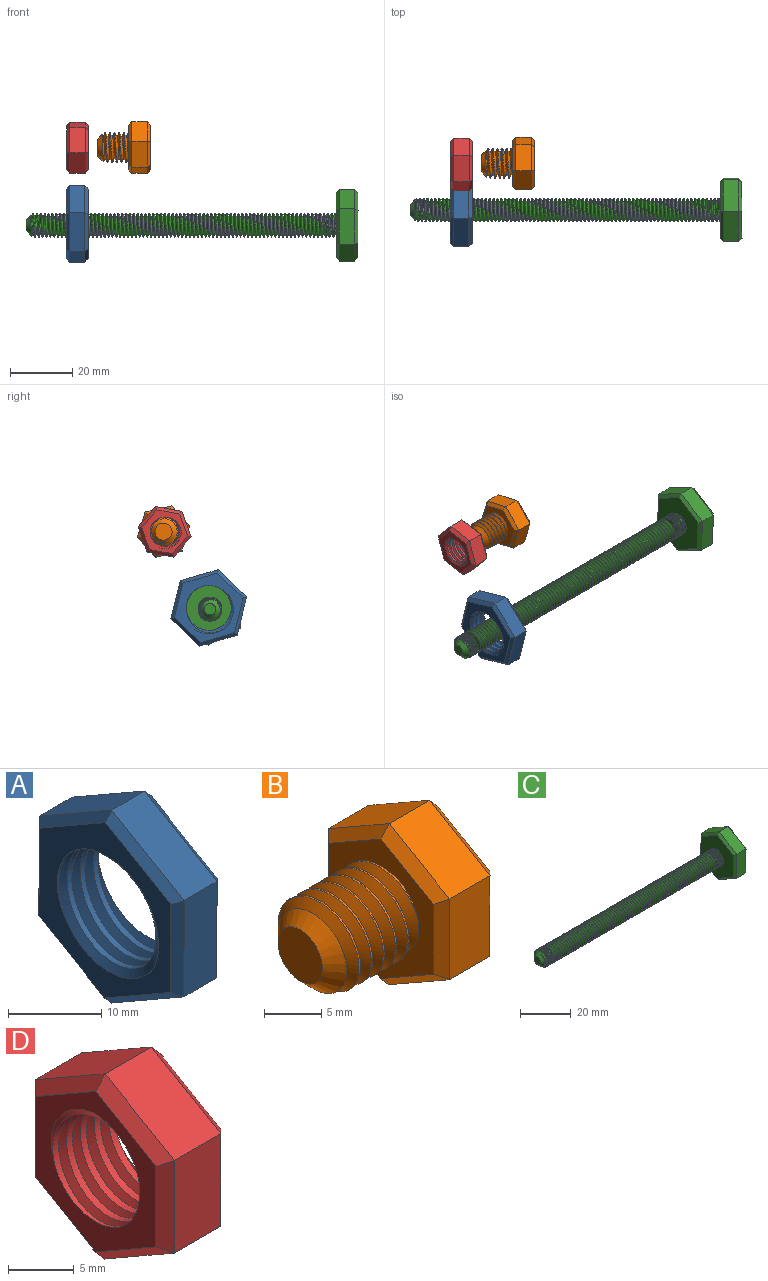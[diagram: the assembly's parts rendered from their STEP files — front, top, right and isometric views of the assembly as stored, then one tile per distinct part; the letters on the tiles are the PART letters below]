
ASSEMBLY  parts=4 mates=2
PART A: 23 faces, bbox 9.3x22.7x26 mm
  f0: cylinder r=7.24mm len=14.48mm, axis (1,0,0), area 111.6mm2, adj f7,f8,f21,f22
  f1: plane 10.98x6.38mm, normal (0,-0.5,0.86), area 63.5mm2, adj f2,f6,f14,f18
  f2: plane 12.7x5mm, normal (0,-1,0), area 63.5mm2, adj f1,f3,f12,f16
  f3: plane 11.02x6.32mm, normal (0,-0.5,-0.87), area 63.5mm2, adj f2,f4,f10,f15
  f4: plane 10.98x6.38mm, normal (0,0.5,-0.86), area 63.5mm2, adj f3,f5,f9,f17
  f5: plane 12.7x5mm, normal (0,1,0), area 63.5mm2, adj f4,f6,f11,f19
  f6: plane 11.02x6.32mm, normal (0,0.5,0.87), area 63.5mm2, adj f1,f5,f13,f20
  f7: plane 23.73x20.67mm, normal (-1,0,0), area 164.4mm2, adj f0,f9,f10,f11,f12,f13,f14,f21
  f8: plane 23.73x20.67mm, normal (1,0,0), area 164.4mm2, adj f0,f15,f16,f17,f18,f19,f20,f21
  f9: plane 10.99x6.96mm, normal (-0.71,0.36,-0.61), area 17.1mm2, adj f4,f7,f10,f11
  f10: plane 11.02x6.9mm, normal (-0.71,-0.35,-0.61), area 17.1mm2, adj f3,f7,f9,f12
  f11: plane 12.7x1.03mm, normal (-0.71,0.71,0), area 17.1mm2, adj f5,f7,f9,f13
  f12: plane 12.7x1.03mm, normal (-0.71,-0.71,0), area 17.1mm2, adj f2,f7,f10,f14
  f13: plane 11.02x6.9mm, normal (-0.71,0.35,0.61), area 17.1mm2, adj f6,f7,f11,f14
  f14: plane 10.99x6.96mm, normal (-0.71,-0.36,0.61), area 17.1mm2, adj f1,f7,f12,f13
  f15: plane 11.02x6.9mm, normal (0.71,-0.35,-0.61), area 17.1mm2, adj f3,f8,f16,f17
  f16: plane 12.7x1.03mm, normal (0.71,-0.71,0), area 17.1mm2, adj f2,f8,f15,f18
  f17: plane 10.99x6.96mm, normal (0.71,0.36,-0.61), area 17.1mm2, adj f4,f8,f15,f19
  f18: plane 10.99x6.96mm, normal (0.71,-0.36,0.61), area 17.1mm2, adj f1,f8,f16,f20
  f19: plane 12.7x1.03mm, normal (0.71,0.71,0), area 17.1mm2, adj f5,f8,f17,f20
  f20: plane 11.02x6.9mm, normal (0.71,0.35,0.61), area 17.1mm2, adj f6,f8,f18,f19
  f21: bspline ~19.31x16.73mm, area 223mm2, adj f0,f7,f8,f22
  f22: bspline ~19.31x16.73mm, area 223mm2, adj f0,f7,f8,f21
PART B: 25 faces, bbox 17.8x15.9x18.1 mm
  f0: cylinder r=4.75mm len=9.5mm, axis (1,0,0), area 28.1mm2, adj f1,f2,f4,f12
  f1: bspline ~10.97x9.91mm, area 196.7mm2, adj f0,f2,f4,f12
  f2: bspline ~10.97x10.66mm, area 196.6mm2, adj f0,f1,f4,f12
  f3: plane 5.5x5.5mm, normal (-1,0,0), area 23.8mm2, adj f4
  f4: cone r=4.75mm half-angle=45deg, axis (1,0,0), area 47.4mm2, adj f0,f1,f2,f3
  f5: plane 7.48x5mm, normal (0,-0.5,0.86), area 43.3mm2, adj f6,f10,f18,f22
  f6: plane 8.66x5mm, normal (0,-1,0), area 43.3mm2, adj f5,f7,f16,f20
  f7: plane 7.52x5mm, normal (0,-0.5,-0.87), area 43.3mm2, adj f6,f8,f14,f19
  f8: plane 7.48x5mm, normal (0,0.5,-0.86), area 43.3mm2, adj f7,f9,f13,f21
  f9: plane 8.66x5mm, normal (0,1,0), area 43.3mm2, adj f8,f10,f15,f23
  f10: plane 7.52x5mm, normal (0,0.5,0.87), area 43.3mm2, adj f5,f9,f17,f24
  f11: plane 15.01x13.03mm, normal (1,0,0), area 146.4mm2, adj f13,f14,f15,f16,f17,f18
  f12: plane 15.83x13.85mm, normal (-1,0,0), area 89.2mm2, adj f0,f1,f2,f19,f20,f21,f22,f23
  f13: plane 7.49x4.93mm, normal (0.71,0.36,-0.61), area 11.4mm2, adj f8,f11,f14,f15
  f14: plane 7.52x4.88mm, normal (0.71,-0.35,-0.61), area 11.4mm2, adj f7,f11,f13,f16
  f15: plane 8.66x1.03mm, normal (0.71,0.71,0), area 11.4mm2, adj f9,f11,f13,f17
  f16: plane 8.66x1.03mm, normal (0.71,-0.71,0), area 11.4mm2, adj f6,f11,f14,f18
  f17: plane 7.52x4.88mm, normal (0.71,0.35,0.61), area 11.4mm2, adj f10,f11,f15,f18
  f18: plane 7.49x4.93mm, normal (0.71,-0.36,0.61), area 11.4mm2, adj f5,f11,f16,f17
  f19: plane 7.52x4.88mm, normal (-0.71,-0.35,-0.61), area 11.4mm2, adj f7,f12,f20,f21
  f20: plane 8.66x1.03mm, normal (-0.71,-0.71,0), area 11.4mm2, adj f6,f12,f19,f22
  f21: plane 7.49x4.93mm, normal (-0.71,0.36,-0.61), area 11.4mm2, adj f8,f12,f19,f23
  f22: plane 7.49x4.93mm, normal (-0.71,-0.36,0.61), area 11.4mm2, adj f5,f12,f20,f24
  f23: plane 8.66x1.03mm, normal (-0.71,0.71,0), area 11.4mm2, adj f9,f12,f21,f24
  f24: plane 7.52x4.88mm, normal (-0.71,0.35,0.61), area 11.4mm2, adj f10,f12,f22,f23
PART C: 25 faces, bbox 107.7x20.7x23.8 mm
  f0: cylinder r=3.84mm len=98mm, axis (1,0,0), area 1496mm2, adj f1,f2,f4,f12
  f1: bspline ~99.71x8.87mm, area 1824.1mm2, adj f0,f2,f4,f12
  f2: bspline ~100.13x8.87mm, area 1829.9mm2, adj f0,f1,f4,f12
  f3: plane 3.68x3.68mm, normal (-1,0,0), area 10.6mm2, adj f4
  f4: cone r=3.84mm half-angle=45deg, axis (1,0,0), area 37.5mm2, adj f0,f1,f2,f3
  f5: plane 9.98x5.81mm, normal (0,-0.5,0.86), area 57.7mm2, adj f6,f10,f18,f22
  f6: plane 11.55x5mm, normal (0,-1,0), area 57.7mm2, adj f5,f7,f16,f20
  f7: plane 10.02x5.74mm, normal (0,-0.5,-0.87), area 57.7mm2, adj f6,f8,f14,f19
  f8: plane 9.98x5.81mm, normal (0,0.5,-0.86), area 57.7mm2, adj f7,f9,f13,f21
  f9: plane 11.55x5mm, normal (0,1,0), area 57.7mm2, adj f8,f10,f15,f23
  f10: plane 10.02x5.74mm, normal (0,0.5,0.87), area 57.7mm2, adj f5,f9,f17,f24
  f11: plane 20.78x18.04mm, normal (1,0,0), area 280.6mm2, adj f13,f14,f15,f16,f17,f18
  f12: plane 21.48x18.73mm, normal (-1,0,0), area 243.4mm2, adj f0,f1,f2,f19,f20,f21,f22,f23
  f13: plane 9.98x6.38mm, normal (0.71,0.36,-0.61), area 15.5mm2, adj f8,f11,f14,f15
  f14: plane 10.02x6.32mm, normal (0.71,-0.35,-0.61), area 15.5mm2, adj f7,f11,f13,f16
  f15: plane 11.55x1.04mm, normal (0.71,0.71,0), area 15.5mm2, adj f9,f11,f13,f17
  f16: plane 11.55x1.04mm, normal (0.71,-0.71,0), area 15.5mm2, adj f6,f11,f14,f18
  f17: plane 10.02x6.32mm, normal (0.71,0.35,0.61), area 15.5mm2, adj f10,f11,f15,f18
  f18: plane 9.98x6.38mm, normal (0.71,-0.36,0.61), area 15.5mm2, adj f5,f11,f16,f17
  f19: plane 10.02x6.32mm, normal (-0.71,-0.35,-0.61), area 15.5mm2, adj f7,f12,f20,f21
  f20: plane 11.55x1.04mm, normal (-0.71,-0.71,0), area 15.5mm2, adj f6,f12,f19,f22
  f21: plane 9.98x6.38mm, normal (-0.71,0.36,-0.61), area 15.5mm2, adj f8,f12,f19,f23
  f22: plane 9.98x6.38mm, normal (-0.71,-0.36,0.61), area 15.5mm2, adj f5,f12,f20,f24
  f23: plane 11.55x1.04mm, normal (-0.71,0.71,0), area 15.5mm2, adj f9,f12,f21,f24
  f24: plane 10.02x6.32mm, normal (-0.71,0.35,0.61), area 15.5mm2, adj f10,f12,f22,f23
PART D: 23 faces, bbox 9.1x15.4x17.7 mm
  f0: plane 7.49x5mm, normal (0,-0.5,0.86), area 43.3mm2, adj f1,f5,f13,f17
  f1: plane 8.66x5mm, normal (0,-1,0), area 43.3mm2, adj f0,f2,f11,f15
  f2: plane 7.51x5mm, normal (0,-0.5,-0.87), area 43.3mm2, adj f1,f3,f9,f14
  f3: plane 7.49x5mm, normal (0,0.5,-0.86), area 43.3mm2, adj f2,f4,f8,f16
  f4: plane 8.66x5mm, normal (0,1,0), area 43.3mm2, adj f3,f5,f10,f18
  f5: plane 7.51x5mm, normal (0,0.5,0.87), area 43.3mm2, adj f0,f4,f12,f19
  f6: plane 15.37x13.38mm, normal (-1,0,0), area 71.4mm2, adj f8,f9,f10,f11,f12,f13,f20,f21
  f7: plane 15.37x13.38mm, normal (1,0,0), area 71.4mm2, adj f14,f15,f16,f17,f18,f19,f20,f21
  f8: plane 7.49x4.93mm, normal (-0.71,0.36,-0.61), area 11.4mm2, adj f3,f6,f9,f10
  f9: plane 7.51x4.89mm, normal (-0.71,-0.35,-0.61), area 11.4mm2, adj f2,f6,f8,f11
  f10: plane 8.66x1.02mm, normal (-0.71,0.71,0), area 11.4mm2, adj f4,f6,f8,f12
  f11: plane 8.66x1.02mm, normal (-0.71,-0.71,0), area 11.4mm2, adj f1,f6,f9,f13
  f12: plane 7.51x4.89mm, normal (-0.71,0.35,0.61), area 11.4mm2, adj f5,f6,f10,f13
  f13: plane 7.49x4.93mm, normal (-0.71,-0.36,0.61), area 11.4mm2, adj f0,f6,f11,f12
  f14: plane 7.51x4.89mm, normal (0.71,-0.35,-0.61), area 11.4mm2, adj f2,f7,f15,f16
  f15: plane 8.66x1.02mm, normal (0.71,-0.71,0), area 11.4mm2, adj f1,f7,f14,f17
  f16: plane 7.49x4.93mm, normal (0.71,0.36,-0.61), area 11.4mm2, adj f3,f7,f14,f18
  f17: plane 7.49x4.93mm, normal (0.71,-0.36,0.61), area 11.4mm2, adj f0,f7,f15,f19
  f18: plane 8.66x1.02mm, normal (0.71,0.71,0), area 11.4mm2, adj f4,f7,f16,f19
  f19: plane 7.51x4.89mm, normal (0.71,0.35,0.61), area 11.4mm2, adj f5,f7,f17,f18
  f20: cylinder r=4.66mm len=9.32mm, axis (1,0,0), area 85.4mm2, adj f6,f7,f21,f22
  f21: bspline ~12.5x10.82mm, area 128.4mm2, adj f6,f7,f20,f22
  f22: bspline ~12.5x10.82mm, area 128.5mm2, adj f6,f7,f20,f21
PLACE A rot(axis=(0,0.6,-0.8),180deg) t=(-55.27,-6.86,23.48)mm fixed
PLACE B rot(axis=(-1,0,0),43.8deg) t=(-31.66,7.73,48.08)mm
PLACE C rot(axis=(-1,0,0),178.1deg) t=(35.23,-7.25,23.06)mm
PLACE D rot(axis=(1,0,0),100.2deg) t=(-48.16,7.38,48.02)mm fixed
MATE cylindrical C.f0 <-> A.f7  axis (-1,0,0) through (-68.27,-7.25,23.06)mm
MATE cylindrical B.f0 <-> D.f6  axis (-1,0,0) through (-45.16,7.73,48.08)mm
